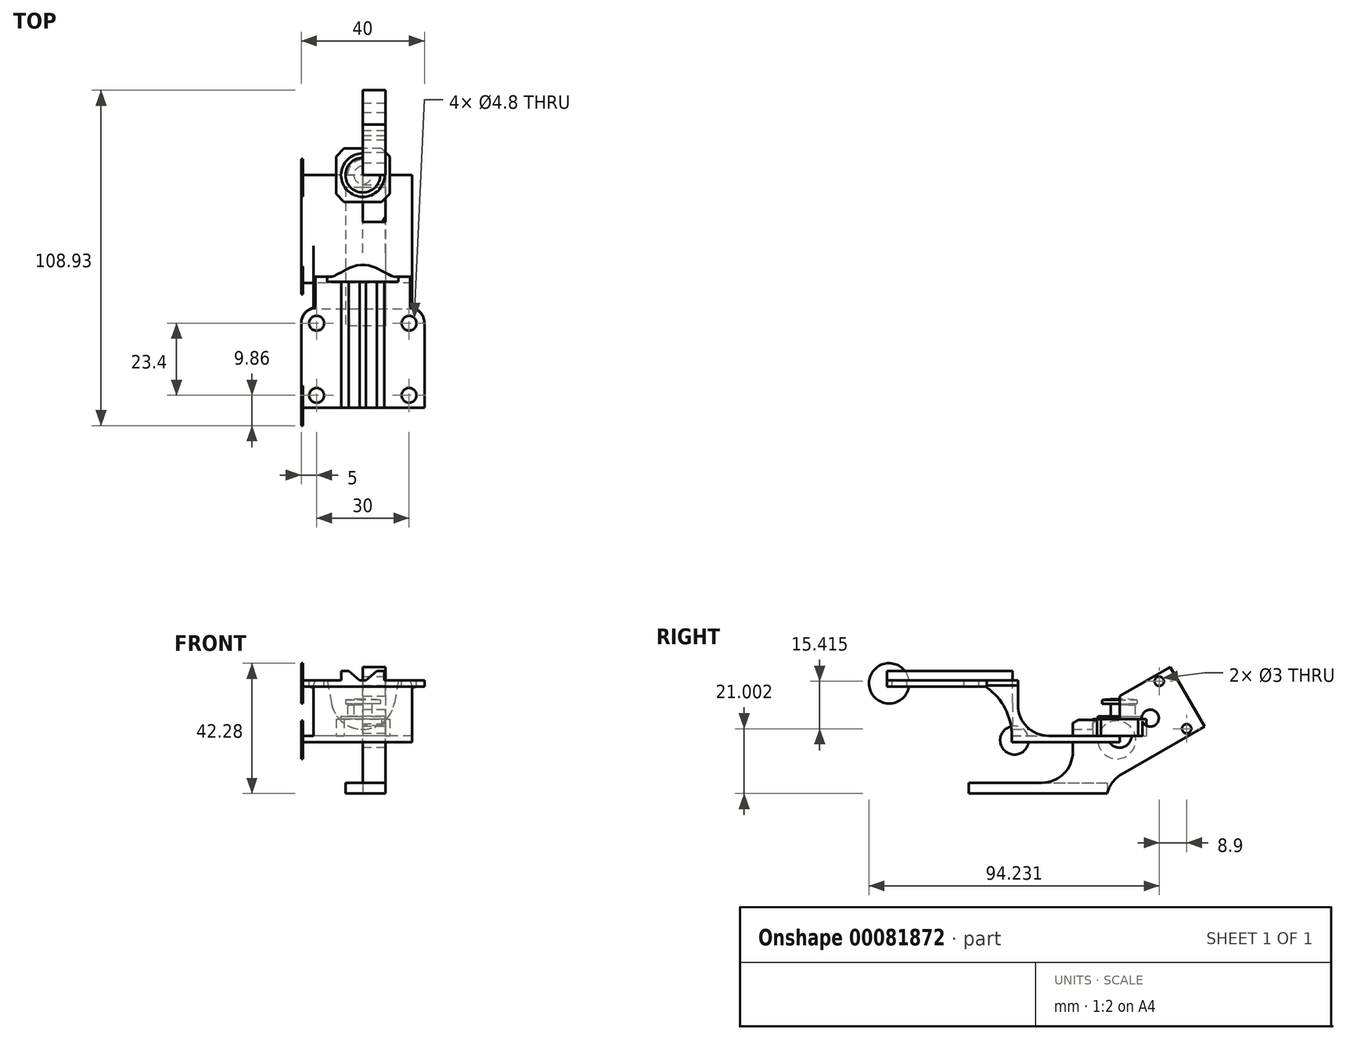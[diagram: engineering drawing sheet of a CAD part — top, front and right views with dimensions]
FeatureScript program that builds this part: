
annotation { "Feature Type Name" : "Feature", "Feature Type Description" : "" }
export const myFeature = defineFeature(function(context is Context, id is Id, definition is map)
    precondition{}
    {
        {
            var Q0;
            Q0=qCreatedBy(makeId("Top.planeOp"),FACE);
            var sketch = newSketch(context, id + "F0", { "sketchPlane" : qUnion([Q0])});
            skCircle(sketch, "E0", {"center": v(0, 0) * mm, "radius": 5 * mm});
            skSolve(sketch);
        }
        {
            var Q0;
            Q0 = qSketchRegion(id + "F0", true);
            extrude(context, id + "F1", {"entities" : qUnion([Q0]), "depth" : 10 * mm, "offsetDistance" : 25 * mm});
        }
        {
            var Q0;
            Q0=qCreatedBy(makeId("Right.planeOp"),FACE);
            var sketch = newSketch(context, id + "F2", { "sketchPlane" : qUnion([Q0])});
            skLineSegment(sketch, "E1", {"start": v(0, 0) * mm, "end": v(17.32, 10) * mm, "construction": true});
            skLineSegment(sketch, "E2", {"start": v(12.87, 17.7) * mm, "end": v(21.77, 2.3) * mm, "construction": true});
            skCircle(sketch, "E3", {"center": v(12.87, 17.7) * mm, "radius": 1.5 * mm});
            skCircle(sketch, "E4", {"center": v(21.77, 2.3) * mm, "radius": 1.5 * mm});
            skLineSegment(sketch, "E5", {"start": v(-15.19, 4.1) * mm, "end": v(16.42, 22.36) * mm});
            skLineSegment(sketch, "E6", {"start": v(16.42, 22.36) * mm, "end": v(27.57, 3.04) * mm});
            skLineSegment(sketch, "E7", {"start": v(27.57, 3.04) * mm, "end": v(-4.04, -15.2) * mm});
            skLineSegment(sketch, "E8", {"start": v(-4.04, -15.2) * mm, "end": v(-15.19, 4.1) * mm});
            skCircle(sketch, "E9", {"center": v(0, 0) * mm, "radius": 3.85 * mm});
            skCircle(sketch, "E10", {"center": v(9.96, 5.75) * mm, "radius": 2.75 * mm});
            skLineSegment(sketch, "E11.bottom", {"start": v(-4.04, -18.7) * mm, "end": v(-49.04, -18.7) * mm});
            skLineSegment(sketch, "E11.top", {"start": v(-4.04, -15.2) * mm, "end": v(-49.04, -15.2) * mm});
            skLineSegment(sketch, "E11.left", {"start": v(-4.04, -18.7) * mm, "end": v(-4.04, -15.2) * mm});
            skLineSegment(sketch, "E11.right", {"start": v(-49.04, -18.7) * mm, "end": v(-49.04, -15.2) * mm});
            skLineSegment(sketch, "E12", {"start": v(-15.19, 4.1) * mm, "end": v(-15.19, -5.2) * mm});
            skArc(sketch, "E13", {"start": v(-25.19, -15.2) * mm, "mid": v(-18.12, -12.28) * mm, "end": v(-15.19, -5.2) * mm});
            skSolve(sketch);
        }
        {
            var Q0;
            Q0 = qSketchRegion(id + "F2", true);
            extrude(context, id + "F3", {"entities" : qUnion([Q0]), "depth" : 7.4 * mm});
        }
        {
            var Q0;
            Q0=makeQuery(id+"F3.opExtrude","CAP_FACE",FACE,{"disambiguationData":[OSD([sQuery(id+"F2.wireOp",EDGE,"E3"),sQuery(id+"F2.wireOp",EDGE,"E4"),sQuery(id+"F2.wireOp",EDGE,"E5"),sQuery(id+"F2.wireOp",EDGE,"E6"),sQuery(id+"F2.wireOp",EDGE,"E7"),sQuery(id+"F2.wireOp",EDGE,"E9"),sQuery(id+"F2.wireOp",EDGE,"E10"),sQuery(id+"F2.wireOp",EDGE,"E11.bottom"),sQuery(id+"F2.wireOp",EDGE,"E11.top"),sQuery(id+"F2.wireOp",EDGE,"E11.left"),sQuery(id+"F2.wireOp",EDGE,"E11.right"),sQuery(id+"F2.wireOp",EDGE,"E12"),sQuery(id+"F2.wireOp",EDGE,"E13")])],"isStart":false});
            var sketch = newSketch(context, id + "F4", { "sketchPlane" : qUnion([Q0])});
            skLineSegment(sketch, "E14.bottom", {"start": v(-49.04, -15.2) * mm, "end": v(-4.04, -15.2) * mm});
            skLineSegment(sketch, "E14.top", {"start": v(-49.04, -18.7) * mm, "end": v(-4.04, -18.7) * mm});
            skLineSegment(sketch, "E14.left", {"start": v(-49.04, -15.2) * mm, "end": v(-49.04, -18.7) * mm});
            skLineSegment(sketch, "E14.right", {"start": v(-4.04, -15.2) * mm, "end": v(-4.04, -18.7) * mm});
            skSolve(sketch);
        }
        {
            var Q0;
            Q0 = qSketchRegion(id + "F4", true);
            extrude(context, id + "F5", {"entities" : qUnion([Q0]), "operationType" : NewBodyOperationType.ADD, "oppositeDirection" : true, "depth" : 5.6 * mm + 7.4 * mm});
        }
        {
            var Q0;
            Q0=makeQuery(id+"F3.opExtrude","SWEPT_EDGE",EDGE,{"disambiguationData":[OSD([sQuery(id+"F2.wireOp",EDGE,"E7"),sQuery(id+"F2.wireOp",EDGE,"E8"),sQuery(id+"F2.wireOp",EDGE,"E11.top"),sQuery(id+"F2.wireOp",EDGE,"E11.left")])]});
            fillet(context, id + "F6", {"entities" : qUnion([Q0]), "radius" : 10 * mm, "tangentPropagation" : true, "allowEdgeOverflow" : false});
        }
        {
            var Q0;
            Q0=qCreatedBy(makeId("Right.planeOp"),FACE);
            var sketch = newSketch(context, id + "F7", { "sketchPlane" : qUnion([Q0])});
            skLineSegment(sketch, "E15.bottom", {"start": v(0, 0) * mm, "end": v(-35, 0) * mm});
            skLineSegment(sketch, "E15.top", {"start": v(0, -2) * mm, "end": v(-35, -2) * mm});
            skLineSegment(sketch, "E15.left", {"start": v(0, 0) * mm, "end": v(0, -2) * mm});
            skLineSegment(sketch, "E15.right", {"start": v(-35, 0) * mm, "end": v(-35, -2) * mm});
            skLineSegment(sketch, "E16.bottom", {"start": v(-35, 0) * mm, "end": v(-33, 0) * mm});
            skLineSegment(sketch, "E16.top", {"start": v(-35, 8) * mm, "end": v(-33, 8) * mm});
            skLineSegment(sketch, "E16.left", {"start": v(-35, 0) * mm, "end": v(-35, 8) * mm});
            skLineSegment(sketch, "E16.right", {"start": v(-33, 0) * mm, "end": v(-33, 8) * mm});
            skArc(sketch, "E17", {"start": v(-33, 10) * mm, "mid": v(-30.07, 2.93) * mm, "end": v(-23, 0) * mm});
            skLineSegment(sketch, "E18.bottom", {"start": v(-33, 10) * mm, "end": v(-35, 10) * mm});
            skLineSegment(sketch, "E18.left", {"start": v(-33, 10) * mm, "end": v(-33, 8) * mm});
            skLineSegment(sketch, "E18.right", {"start": v(-35, 10) * mm, "end": v(-35, 8) * mm});
            skLineSegment(sketch, "E19.bottom", {"start": v(-75.5, 18) * mm, "end": v(-43.5, 18) * mm});
            skLineSegment(sketch, "E19.top", {"start": v(-75.5, 16) * mm, "end": v(-43.5, 16) * mm});
            skLineSegment(sketch, "E19.left", {"start": v(-75.5, 18) * mm, "end": v(-75.5, 16) * mm});
            skLineSegment(sketch, "E19.right", {"start": v(-43.5, 18) * mm, "end": v(-43.5, 16) * mm});
            skLineSegment(sketch, "E20.top", {"start": v(-33, 18) * mm, "end": v(-35, 18) * mm});
            skLineSegment(sketch, "E20.left", {"start": v(-33, 10) * mm, "end": v(-33, 18) * mm});
            skLineSegment(sketch, "E20.right", {"start": v(-35, 10) * mm, "end": v(-35, 18) * mm});
            skLineSegment(sketch, "E21.bottom", {"start": v(-43.5, 18) * mm, "end": v(-35, 18) * mm});
            skLineSegment(sketch, "E21.top", {"start": v(-43.5, 16) * mm, "end": v(-35, 16) * mm});
            skLineSegment(sketch, "E21.right", {"start": v(-35, 18) * mm, "end": v(-35, 16) * mm});
            skArc(sketch, "E22", {"start": v(-35, 0) * mm, "mid": v(-37.26, 9.06) * mm, "end": v(-43.5, 16) * mm});
            skSolve(sketch);
        }
        {
            var Q0;
            Q0 = qSketchRegion(id + "F7", true);
            extrude(context, id + "F8", {"entities" : qUnion([Q0]), "endBound" : BoundingType.SYMMETRIC, "depth" : 40 * mm});
        }
        {
            var Q0;
            Q0=qCreatedBy(makeId("Front.planeOp"),FACE);
            var sketch = newSketch(context, id + "F9", { "sketchPlane" : qUnion([Q0])});
            skCircle(sketch, "E23", {"center": v(0, 12.5) * mm, "radius": 10.4 * mm});
            skLineSegment(sketch, "E24", {"start": v(-10.24, 10.7) * mm, "end": v(-13.1, 26.96) * mm});
            skLineSegment(sketch, "E25", {"start": v(0, 12.5) * mm, "end": v(0, 30.75) * mm, "construction": true});
            skLineSegment(sketch, "E26.MirrorCS", {"start": v(10.24, 10.7) * mm, "end": v(13.1, 26.96) * mm});
            skLineSegment(sketch, "E27", {"start": v(-13.1, 26.96) * mm, "end": v(13.1, 26.96) * mm});
            skSolve(sketch);
        }
        {
            var Q0;
            Q0 = qSketchRegion(id + "F9", true);
            extrude(context, id + "F10", {"entities" : qUnion([Q0]), "operationType" : NewBodyOperationType.REMOVE, "depth" : 34.7 * mm});
        }
        {
            var Q0;
            Q0=makeQuery(id+"F8.opExtrude","SWEPT_FACE",FACE,{"disambiguationData":[OSD([sQuery(id+"F7.wireOp",EDGE,"E19.bottom"),sQuery(id+"F7.wireOp",EDGE,"E20.top"),sQuery(id+"F7.wireOp",EDGE,"E21.bottom")])]});
            var sketch = newSketch(context, id + "F11", { "sketchPlane" : qUnion([Q0])});
            skLineSegment(sketch, "E28.bottom", {"start": v(15, -48.1) * mm, "end": v(-15, -48.1) * mm, "construction": true});
            skLineSegment(sketch, "E28.top", {"start": v(15, -71.5) * mm, "end": v(-15, -71.5) * mm, "construction": true});
            skLineSegment(sketch, "E28.left", {"start": v(15, -48.1) * mm, "end": v(15, -71.5) * mm, "construction": true});
            skLineSegment(sketch, "E28.right", {"start": v(-15, -48.1) * mm, "end": v(-15, -71.5) * mm, "construction": true});
            skPoint(sketch, "E28.middle", {"position": v(0, -59.8) * mm});
            skPoint(sketch, "E28.middle.positionSnap0", {"position": v(0, -75.5) * mm});
            skPoint(sketch, "E28.centerSnap0", {"position": v(0, -75.5) * mm});
            skCircle(sketch, "E29", {"center": v(-15, -48.1) * mm, "radius": 2.4 * mm});
            skCircle(sketch, "E30", {"center": v(15, -48.1) * mm, "radius": 2.4 * mm});
            skCircle(sketch, "E31", {"center": v(15, -71.5) * mm, "radius": 2.4 * mm});
            skCircle(sketch, "E32", {"center": v(-15, -71.5) * mm, "radius": 2.4 * mm});
            skSolve(sketch);
        }
        {
            var Q0;
            Q0 = qSketchRegion(id + "F11", true);
            extrude(context, id + "F12", {"entities" : qUnion([Q0]), "operationType" : NewBodyOperationType.REMOVE, "oppositeDirection" : true, "depth" : 25 * mm});
        }
        {
            var Q0;
            Q0=makeQuery(id+"F8.opExtrude","SWEPT_FACE",FACE,{"disambiguationData":[OSD([sQuery(id+"F7.wireOp",EDGE,"E19.bottom"),sQuery(id+"F7.wireOp",EDGE,"E20.top"),sQuery(id+"F7.wireOp",EDGE,"E21.bottom")])]});
            var sketch = newSketch(context, id + "F13", { "sketchPlane" : qUnion([Q0])});
            skLineSegment(sketch, "E33.bottom", {"start": v(-7, -34.7) * mm, "end": v(-5, -34.7) * mm});
            skLineSegment(sketch, "E33.top", {"start": v(-7, -75.5) * mm, "end": v(-5, -75.5) * mm});
            skLineSegment(sketch, "E33.left", {"start": v(-7, -34.7) * mm, "end": v(-7, -75.5) * mm});
            skLineSegment(sketch, "E33.right", {"start": v(-5, -34.7) * mm, "end": v(-5, -75.5) * mm});
            skLineSegment(sketch, "E34", {"start": v(0, -34.7) * mm, "end": v(0, -14.12) * mm, "construction": true});
            skLineSegment(sketch, "E35.MirrorCS", {"start": v(7, -34.7) * mm, "end": v(5, -34.7) * mm});
            skLineSegment(sketch, "E36.MirrorCS", {"start": v(7, -75.5) * mm, "end": v(5, -75.5) * mm});
            skLineSegment(sketch, "E37.MirrorCS", {"start": v(7, -34.7) * mm, "end": v(7, -75.5) * mm});
            skLineSegment(sketch, "E38.MirrorCS", {"start": v(5, -34.7) * mm, "end": v(5, -75.5) * mm});
            skSolve(sketch);
        }
        {
            var Q0;
            Q0 = qSketchRegion(id + "F13", true);
            extrude(context, id + "F14", {"entities" : qUnion([Q0]), "operationType" : NewBodyOperationType.ADD, "depth" : 3 * mm});
        }
        {
            var Q0;
            Q0=qCreatedBy(makeId("Front.planeOp"),FACE);
            var sketch = newSketch(context, id + "F15", { "sketchPlane" : qUnion([Q0])});
            skLineSegment(sketch, "E39.bottom", {"start": v(16, -13.45) * mm, "end": v(-16, -13.45) * mm});
            skLineSegment(sketch, "E39.top", {"start": v(16, 16.3) * mm, "end": v(-16, 16.3) * mm});
            skLineSegment(sketch, "E39.left", {"start": v(16, -13.45) * mm, "end": v(16, 16.3) * mm});
            skLineSegment(sketch, "E39.right", {"start": v(-16, -13.45) * mm, "end": v(-16, 16.3) * mm});
            skPoint(sketch, "E39.middle", {"position": v(0, 1.42) * mm});
            skCircle(sketch, "E40", {"center": v(0, 0) * mm, "radius": 56 * mm});
            skLineSegment(sketch, "E41.bottom", {"start": v(13.5, 23.3) * mm, "end": v(-13.5, 23.3) * mm});
            skLineSegment(sketch, "E41.top", {"start": v(13.5, -23.3) * mm, "end": v(-13.5, -23.3) * mm});
            skLineSegment(sketch, "E41.left", {"start": v(13.5, 23.3) * mm, "end": v(13.5, -23.3) * mm});
            skLineSegment(sketch, "E41.right", {"start": v(-13.5, 23.3) * mm, "end": v(-13.5, -23.3) * mm});
            skLineSegment(sketch, "E42", {"start": v(-13.5, 23.3) * mm, "end": v(-16, 16.3) * mm});
            skLineSegment(sketch, "E43", {"start": v(13.5, 23.3) * mm, "end": v(16, 16.3) * mm});
            skSolve(sketch);
        }
        {
            var Q0;
            Q0 = qSketchRegion(id + "F15", true);
            extrude(context, id + "F16", {"entities" : qUnion([Q0]), "operationType" : NewBodyOperationType.REMOVE, "depth" : 37.1 * mm + 6 * mm});
        }
        {
            var Q0;
            Q0=makeQuery(id+"F16.boolean.opBoolean","INTERSECT",EDGE,{"derivedFrom":[makeQuery(id+"F8.opExtrude","CAP_FACE",FACE,{"disambiguationData":[OSD([sQuery(id+"F7.wireOp",EDGE,"E15.bottom"),sQuery(id+"F7.wireOp",EDGE,"E15.top"),sQuery(id+"F7.wireOp",EDGE,"E15.left"),sQuery(id+"F7.wireOp",EDGE,"E15.right"),sQuery(id+"F7.wireOp",EDGE,"E17"),sQuery(id+"F7.wireOp",EDGE,"E19.bottom"),sQuery(id+"F7.wireOp",EDGE,"E19.top"),sQuery(id+"F7.wireOp",EDGE,"E19.left"),sQuery(id+"F7.wireOp",EDGE,"E20.top"),sQuery(id+"F7.wireOp",EDGE,"E20.left"),sQuery(id+"F7.wireOp",EDGE,"E21.bottom"),sQuery(id+"F7.wireOp",EDGE,"E22")])],"isStart":true}),makeQuery(id+"F16.opExtrude","CAP_FACE",FACE,{"disambiguationData":[OSD([sQuery(id+"F15.wireOp",EDGE,"E39.bottom"),sQuery(id+"F15.wireOp",EDGE,"E39.left"),sQuery(id+"F15.wireOp",EDGE,"E39.right"),sQuery(id+"F15.wireOp",EDGE,"E40"),sQuery(id+"F15.wireOp",EDGE,"E41.bottom"),sQuery(id+"F15.wireOp",EDGE,"E41.top"),sQuery(id+"F15.wireOp",EDGE,"E41.left"),sQuery(id+"F15.wireOp",EDGE,"E41.right"),sQuery(id+"F15.wireOp",EDGE,"E42"),sQuery(id+"F15.wireOp",EDGE,"E43")])],"isStart":false})]});
            var Q1;
            Q1=makeQuery(id+"F16.boolean.opBoolean","INTERSECT",EDGE,{"derivedFrom":[makeQuery(id+"F8.opExtrude","CAP_FACE",FACE,{"disambiguationData":[OSD([sQuery(id+"F7.wireOp",EDGE,"E15.bottom"),sQuery(id+"F7.wireOp",EDGE,"E15.top"),sQuery(id+"F7.wireOp",EDGE,"E15.left"),sQuery(id+"F7.wireOp",EDGE,"E15.right"),sQuery(id+"F7.wireOp",EDGE,"E17"),sQuery(id+"F7.wireOp",EDGE,"E19.bottom"),sQuery(id+"F7.wireOp",EDGE,"E19.top"),sQuery(id+"F7.wireOp",EDGE,"E19.left"),sQuery(id+"F7.wireOp",EDGE,"E20.top"),sQuery(id+"F7.wireOp",EDGE,"E20.left"),sQuery(id+"F7.wireOp",EDGE,"E21.bottom"),sQuery(id+"F7.wireOp",EDGE,"E22")])],"isStart":false}),makeQuery(id+"F16.opExtrude","CAP_FACE",FACE,{"disambiguationData":[OSD([sQuery(id+"F15.wireOp",EDGE,"E39.bottom"),sQuery(id+"F15.wireOp",EDGE,"E39.left"),sQuery(id+"F15.wireOp",EDGE,"E39.right"),sQuery(id+"F15.wireOp",EDGE,"E40"),sQuery(id+"F15.wireOp",EDGE,"E41.bottom"),sQuery(id+"F15.wireOp",EDGE,"E41.top"),sQuery(id+"F15.wireOp",EDGE,"E41.left"),sQuery(id+"F15.wireOp",EDGE,"E41.right"),sQuery(id+"F15.wireOp",EDGE,"E42"),sQuery(id+"F15.wireOp",EDGE,"E43")])],"isStart":false})]});
            fillet(context, id + "F17", {"entities" : qUnion([Q0, Q1]), "radius" : 5 * mm, "tangentPropagation" : true, "allowEdgeOverflow" : false});
        }
        {
            var Q0;
            Q0=makeQuery(id+"F14.opExtrude","CAP_EDGE",EDGE,{"disambiguationData":[OSD([sQuery(id+"F13.wireOp",EDGE,"E38.MirrorCS")])],"isStart":true});
            var Q1;
            Q1=makeQuery(id+"F14.opExtrude","CAP_EDGE",EDGE,{"disambiguationData":[OSD([sQuery(id+"F13.wireOp",EDGE,"E33.right")])],"isStart":true});
            chamfer(context, id + "F18", {"entities" : qUnion([Q0, Q1]), "chamferType" : ChamferType.OFFSET_ANGLE, "width" : 4 * mm, "oppositeDirection" : true, "angle" : 40 * degree, "tangentPropagation" : true});
        }
        {
            var Q0;
            Q0=makeQuery(id+"F16.boolean.opBoolean","COPY",FACE,{"derivedFrom":makeQuery(id+"F16.opExtrude","SWEPT_FACE",FACE,{"disambiguationData":[OSD([sQuery(id+"F15.wireOp",EDGE,"E39.right")])]})});
            var sketch = newSketch(context, id + "F19", { "sketchPlane" : qUnion([Q0])});
            skLineSegment(sketch, "E44.bottom", {"start": v(0, -2) * mm, "end": v(35, -2) * mm});
            skLineSegment(sketch, "E44.top", {"start": v(0, 0) * mm, "end": v(35, 0) * mm});
            skLineSegment(sketch, "E44.left", {"start": v(0, -2) * mm, "end": v(0, 0) * mm});
            skLineSegment(sketch, "E44.right", {"start": v(35, -2) * mm, "end": v(35, 0) * mm});
            skSolve(sketch);
        }
        {
            var Q0;
            Q0 = qSketchRegion(id + "F19", true);
            var Q1;
            Q1=makeQuery(id+"F8.opExtrude","CAP_FACE",FACE,{"disambiguationData":[OSD([sQuery(id+"F7.wireOp",EDGE,"E15.bottom"),sQuery(id+"F7.wireOp",EDGE,"E15.top"),sQuery(id+"F7.wireOp",EDGE,"E15.left"),sQuery(id+"F7.wireOp",EDGE,"E15.right"),sQuery(id+"F7.wireOp",EDGE,"E17"),sQuery(id+"F7.wireOp",EDGE,"E19.bottom"),sQuery(id+"F7.wireOp",EDGE,"E19.top"),sQuery(id+"F7.wireOp",EDGE,"E19.left"),sQuery(id+"F7.wireOp",EDGE,"E20.top"),sQuery(id+"F7.wireOp",EDGE,"E20.left"),sQuery(id+"F7.wireOp",EDGE,"E21.bottom"),sQuery(id+"F7.wireOp",EDGE,"E22")])],"isStart":true});
            extrude(context, id + "F20", {"entities" : qUnion([Q0]), "operationType" : NewBodyOperationType.ADD, "endBound" : BoundingType.UP_TO_SURFACE, "endBoundEntityFace" : qUnion([Q1]), "depth" : 25 * mm});
        }
        {
            var Q0;
            Q0=makeQuery(id+"F20.opExtrude","CAP_FACE",FACE,{"disambiguationData":[OSD([sQuery(id+"F19.wireOp",EDGE,"E44.bottom"),sQuery(id+"F19.wireOp",EDGE,"E44.top"),sQuery(id+"F19.wireOp",EDGE,"E44.left"),sQuery(id+"F19.wireOp",EDGE,"E44.right")])],"isStart":false});
            var sketch = newSketch(context, id + "F21", { "sketchPlane" : qUnion([Q0])});
            skCircle(sketch, "E45", {"center": v(0.92, -1.3) * mm, "radius": 6.17 * mm});
            skCircle(sketch, "E46", {"center": v(34.14, -1.45) * mm, "radius": 4.63 * mm});
            skCircle(sketch, "E47", {"center": v(74.82, 17.04) * mm, "radius": 6.53 * mm});
            skSolve(sketch);
        }
        {
            var Q0;
            Q0 = qSketchRegion(id + "F21", true);
            extrude(context, id + "F22", {"entities" : qUnion([Q0]), "operationType" : NewBodyOperationType.ADD, "oppositeDirection" : true, "depth" : .6 * mm});
        }
        {
            var Q0;
            Q0=qCreatedBy(makeId("Top.planeOp"),FACE);
            var sketch = newSketch(context, id + "F23", { "sketchPlane" : qUnion([Q0])});
            skLineSegment(sketch, "E48.bottom", {"start": v(8.7, 8.7) * mm, "end": v(-8.7, 8.7) * mm});
            skLineSegment(sketch, "E48.top", {"start": v(8.7, -8.7) * mm, "end": v(-8.7, -8.7) * mm});
            skLineSegment(sketch, "E48.left", {"start": v(8.7, 8.7) * mm, "end": v(8.7, -8.7) * mm});
            skLineSegment(sketch, "E48.right", {"start": v(-8.7, 8.7) * mm, "end": v(-8.7, -8.7) * mm});
            skPoint(sketch, "E48.middle", {"position": v(0, 0) * mm});
            skLineSegment(sketch, "E49", {"start": v(6.06, 8.7) * mm, "end": v(8.7, 6.06) * mm});
            skLineSegment(sketch, "E50", {"start": v(-8.7, 6.06) * mm, "end": v(-6.06, 8.7) * mm});
            skLineSegment(sketch, "E51", {"start": v(-8.7, -6.06) * mm, "end": v(-6.06, -8.7) * mm});
            skLineSegment(sketch, "E52", {"start": v(6.06, -8.7) * mm, "end": v(8.7, -6.06) * mm});
            skSolve(sketch);
        }
        {
            var Q0;
            {var subQ3=sQuery(id+"F23.wireOp",EDGE,"E49");Q0=makeQuery(id+"F23.imprint","IMPRINT",FACE,{"disambiguationData":[TD([[makeQuery(id+"F23.imprint","IMPRINT",EDGE,{"derivedFrom":subQ3}),-1.0]])]});}
            extrude(context, id + "F24", {"entities" : qUnion([Q0]), "depth" : 5.5 * mm});
        }
        {
            var Q0;
            Q0=makeQuery(id+"F24.opExtrude","CAP_FACE",FACE,{"disambiguationData":[OSD([sQuery(id+"F23.wireOp",EDGE,"E48.bottom"),sQuery(id+"F23.wireOp",EDGE,"E48.top"),sQuery(id+"F23.wireOp",EDGE,"E48.left"),sQuery(id+"F23.wireOp",EDGE,"E48.right"),sQuery(id+"F23.wireOp",EDGE,"E49"),sQuery(id+"F23.wireOp",EDGE,"E50"),sQuery(id+"F23.wireOp",EDGE,"E51"),sQuery(id+"F23.wireOp",EDGE,"E52")])],"isStart":true});
            var sketch = newSketch(context, id + "F25", { "sketchPlane" : qUnion([Q0])});
            skCircle(sketch, "E53", {"center": v(-6.08, 6.08) * mm, "radius": 0.7 * mm});
            skLineSegment(sketch, "E54", {"start": v(-7.38, -7.38) * mm, "end": v(7.38, 7.38) * mm, "construction": true});
            skLineSegment(sketch, "E55", {"start": v(-6.08, 6.08) * mm, "end": v(0, 0) * mm, "construction": true});
            skCircle(sketch, "E56.MirrorC", {"center": v(6.08, -6.08) * mm, "radius": 0.7 * mm});
            skSolve(sketch);
        }
        {
            var Q0;
            Q0 = qSketchRegion(id + "F25", true);
            extrude(context, id + "F26", {"entities" : qUnion([Q0]), "operationType" : NewBodyOperationType.ADD, "depth" : 1.3 * mm});
        }
        {
            var Q0;
            Q0=qCreatedBy(makeId("Front.planeOp"),FACE);
            var sketch = newSketch(context, id + "F27", { "sketchPlane" : qUnion([Q0])});
            skLineSegment(sketch, "E57", {"start": v(0, 0) * mm, "end": v(0, 11.92) * mm});
            skArc(sketch, "E58", {"start": v(5.65, 11.64) * mm, "mid": v(2.83, 11.85) * mm, "end": v(0, 11.92) * mm});
            skLineSegment(sketch, "E59", {"start": v(0, 11.92) * mm, "end": v(7.63, 11.92) * mm, "construction": true});
            skLineSegment(sketch, "E60", {"start": v(5.65, 11.64) * mm, "end": v(5.65, 10.4) * mm});
            skLineSegment(sketch, "E61", {"start": v(5.65, 10.4) * mm, "end": v(2.9, 10.4) * mm});
            skLineSegment(sketch, "E62", {"start": v(2.9, 10.4) * mm, "end": v(2.9, 6.32) * mm});
            skLineSegment(sketch, "E63", {"start": v(2.9, 6.32) * mm, "end": v(7.07, 6.32) * mm});
            skLineSegment(sketch, "E64", {"start": v(7.07, 6.32) * mm, "end": v(7.07, 0) * mm});
            skLineSegment(sketch, "E65", {"start": v(7.07, 0) * mm, "end": v(0, 0) * mm});
            skSolve(sketch);
        }
        {
            var Q0;
            Q0=makeQuery(id+"F27.imprint","IMPRINT",FACE,{"disambiguationData":[TD([[makeQuery(id+"F27.imprint","IMPRINT",EDGE,{"derivedFrom":sQuery(id+"F27.wireOp",EDGE,"E57")}),-1.0]])]});
            var Q1;
            Q1=sQuery(id+"F27.wireOp",EDGE,"E58");
            var Q2;
            Q2=sQuery(id+"F27.wireOp",EDGE,"E60");
            var Q3;
            Q3=sQuery(id+"F27.wireOp",EDGE,"E61");
            var Q4;
            Q4=sQuery(id+"F27.wireOp",EDGE,"E62");
            var Q5;
            Q5=sQuery(id+"F27.wireOp",EDGE,"E63");
            var Q6;
            Q6=sQuery(id+"F27.wireOp",EDGE,"E64");
            var Q7;
            Q7=sQuery(id+"F27.wireOp",EDGE,"E65");
            var Q8;
            Q8=sQuery(id+"F27.wireOp",EDGE,"E57");
            revolve(context, id + "F28", {"operationType" : NewBodyOperationType.ADD, "entities" : qUnion([Q0]), "surfaceEntities" : qUnion([Q1, Q2, Q3, Q4, Q5, Q6, Q7]), "axis" : qUnion([Q8]), "revolveType" : RevolveType.FULL});
        }
    });
